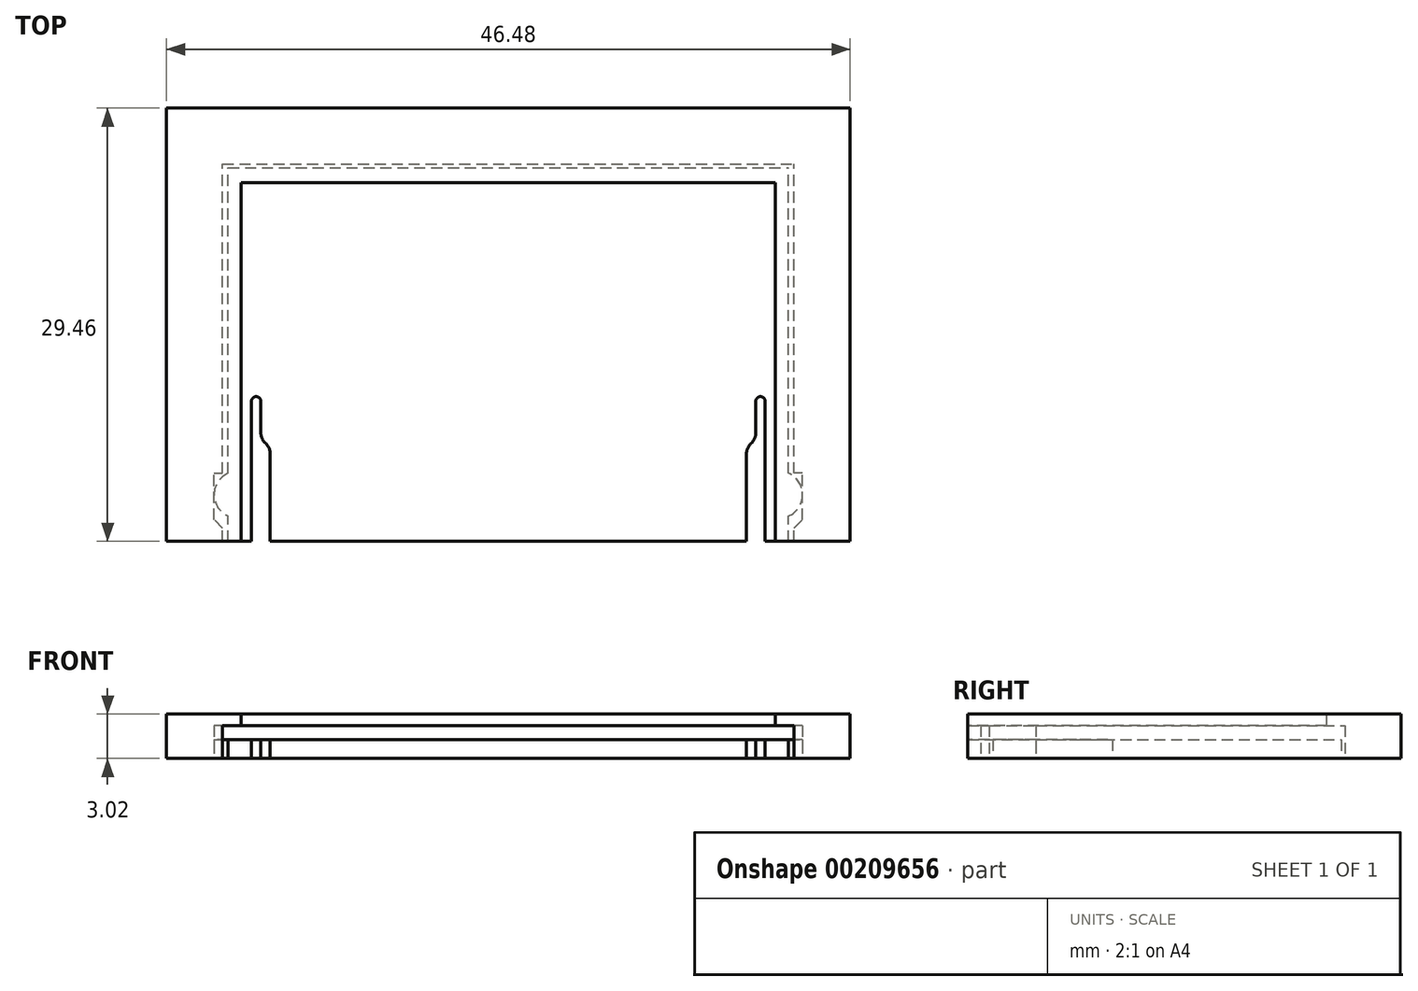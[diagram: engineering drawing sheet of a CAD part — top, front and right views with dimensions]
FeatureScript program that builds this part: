
annotation { "Feature Type Name" : "Feature", "Feature Type Description" : "" }
export const myFeature = defineFeature(function(context is Context, id is Id, definition is map)
    precondition{}
    {
        {
            var Q0;
            Q0=qCreatedBy(makeId("Top.planeOp"),FACE);
            var sketch = newSketch(context, id + "F0", { "sketchPlane" : qUnion([Q0])});
            skLineSegment(sketch, "E0", {"start": v(0, 0) * mm, "end": v(0, -25.4) * mm});
            skLineSegment(sketch, "E1", {"start": v(0, -25.4) * mm, "end": v(-16.2, -25.4) * mm});
            skLineSegment(sketch, "E2", {"start": v(-16.2, -25.4) * mm, "end": v(-16.2, -19.44) * mm});
            skLineSegment(sketch, "E3", {"start": v(-16.47, -18.77) * mm, "end": v(-16.55, -18.7) * mm});
            skLineSegment(sketch, "E4", {"start": v(-16.83, -18.02) * mm, "end": v(-16.83, -15.88) * mm});
            skLineSegment(sketch, "E5", {"start": v(-16.83, -15.88) * mm, "end": v(-17.46, -15.88) * mm, "construction": true});
            skLineSegment(sketch, "E6", {"start": v(-17.46, -15.88) * mm, "end": v(-17.46, -25.4) * mm});
            skLineSegment(sketch, "E7", {"start": v(-17.46, -25.4) * mm, "end": v(-19.05, -25.4) * mm});
            skLineSegment(sketch, "E8", {"start": v(-19.05, -25.4) * mm, "end": v(-19.05, -23.68) * mm});
            skLineSegment(sketch, "E9", {"start": v(-19.05, -20.77) * mm, "end": v(-19.05, 0) * mm});
            skLineSegment(sketch, "E10", {"start": v(-19.05, 0) * mm, "end": v(0, 0) * mm});
            skArc(sketch, "E11", {"start": v(-19.05, -20.77) * mm, "mid": v(-20, -22.23) * mm, "end": v(-19.05, -23.68) * mm});
            skArc(sketch, "E12", {"start": v(-16.83, -15.88) * mm, "mid": v(-17.14, -15.56) * mm, "end": v(-17.46, -15.88) * mm});
            skPoint(sketch, "E13.visualSharp", {"position": v(-16.83, -18.41) * mm});
            skArc(sketch, "E13.filletArc", {"start": v(-16.83, -18.02) * mm, "mid": v(-16.75, -18.38) * mm, "end": v(-16.55, -18.7) * mm});
            skPoint(sketch, "E14.visualSharp", {"position": v(-16.2, -19.05) * mm});
            skArc(sketch, "E14.filletArc", {"start": v(-16.2, -19.44) * mm, "mid": v(-16.27, -19.08) * mm, "end": v(-16.47, -18.77) * mm});
            skSolve(sketch);
        }
        {
            var Q0;
            Q0 = qSketchRegion(id + "F0", true);
            extrude(context, id + "F1", {"entities" : qUnion([Q0]), "depth" : 1.27 * mm});
        }
        {
            var Q0;
            Q0=qCreatedBy(makeId("Top.planeOp"),FACE);
            var sketch = newSketch(context, id + "F2", { "sketchPlane" : qUnion([Q0])});
            skLineSegment(sketch, "E15", {"start": v(-19.43, -25.4) * mm, "end": v(-19.43, -24.5) * mm});
            skLineSegment(sketch, "E16", {"start": v(-19.43, -24.5) * mm, "end": v(-20, -23.93) * mm});
            skLineSegment(sketch, "E17", {"start": v(-20, -23.93) * mm, "end": v(-20, -20.77) * mm});
            skLineSegment(sketch, "E18", {"start": v(-20, -20.77) * mm, "end": v(-19.43, -20.77) * mm});
            skLineSegment(sketch, "E19", {"start": v(-19.43, -20.77) * mm, "end": v(-19.43, 0.25) * mm});
            skLineSegment(sketch, "E20", {"start": v(-19.43, 0.25) * mm, "end": v(0, 0.25) * mm});
            skLineSegment(sketch, "E21", {"start": v(0, 0.25) * mm, "end": v(0, 4.06) * mm});
            skLineSegment(sketch, "E22", {"start": v(0, 4.06) * mm, "end": v(-23.24, 4.06) * mm});
            skLineSegment(sketch, "E23", {"start": v(-23.24, 4.06) * mm, "end": v(-23.24, -25.4) * mm});
            skLineSegment(sketch, "E24", {"start": v(-23.24, -25.4) * mm, "end": v(-19.43, -25.4) * mm});
            skSolve(sketch);
        }
        {
            var Q0;
            Q0 = qSketchRegion(id + "F2", true);
            extrude(context, id + "F3", {"entities" : qUnion([Q0]), "depth" : 2.22 * mm});
        }
        {
            var Q0;
            Q0=makeQuery(id+"F3.opExtrude","CAP_FACE",FACE,{"disambiguationData":[OSD([sQuery(id+"F2.wireOp",EDGE,"E15"),sQuery(id+"F2.wireOp",EDGE,"E16"),sQuery(id+"F2.wireOp",EDGE,"E17"),sQuery(id+"F2.wireOp",EDGE,"E18"),sQuery(id+"F2.wireOp",EDGE,"E19"),sQuery(id+"F2.wireOp",EDGE,"E20"),sQuery(id+"F2.wireOp",EDGE,"E21"),sQuery(id+"F2.wireOp",EDGE,"E22"),sQuery(id+"F2.wireOp",EDGE,"E23"),sQuery(id+"F2.wireOp",EDGE,"E24")])],"isStart":false});
            var sketch = newSketch(context, id + "F4", { "sketchPlane" : qUnion([Q0])});
            skLineSegment(sketch, "E25", {"start": v(0, 4.06) * mm, "end": v(0, -1.02) * mm});
            skLineSegment(sketch, "E26", {"start": v(0, -1.02) * mm, "end": v(-18.16, -1.02) * mm});
            skLineSegment(sketch, "E27", {"start": v(-18.16, -1.02) * mm, "end": v(-18.16, -25.4) * mm});
            skLineSegment(sketch, "E28", {"start": v(-18.16, -25.4) * mm, "end": v(-23.24, -25.4) * mm});
            skLineSegment(sketch, "E29", {"start": v(-23.24, -25.4) * mm, "end": v(-23.24, 4.06) * mm});
            skLineSegment(sketch, "E30", {"start": v(-23.24, 4.06) * mm, "end": v(0, 4.06) * mm});
            skSolve(sketch);
        }
        {
            var Q0;
            Q0 = qSketchRegion(id + "F4", true);
            extrude(context, id + "F5", {"entities" : qUnion([Q0]), "operationType" : NewBodyOperationType.ADD, "depth" : 0.8 * mm});
        }
        {
            var Q0;
            Q0=makeQuery(id+"F1.opExtrude","SWEPT_BODY",BODY,{"disambiguationData":[OSD([sQuery(id+"F0.wireOp",EDGE,"E0"),sQuery(id+"F0.wireOp",EDGE,"E1"),sQuery(id+"F0.wireOp",EDGE,"E2"),sQuery(id+"F0.wireOp",EDGE,"E3"),sQuery(id+"F0.wireOp",EDGE,"E4"),sQuery(id+"F0.wireOp",EDGE,"E6"),sQuery(id+"F0.wireOp",EDGE,"E7"),sQuery(id+"F0.wireOp",EDGE,"E8"),sQuery(id+"F0.wireOp",EDGE,"E9"),sQuery(id+"F0.wireOp",EDGE,"E10"),sQuery(id+"F0.wireOp",EDGE,"E11"),sQuery(id+"F0.wireOp",EDGE,"E12"),sQuery(id+"F0.wireOp",EDGE,"E13.filletArc"),sQuery(id+"F0.wireOp",EDGE,"E14.filletArc")])]});
            var Q1;
            Q1=qCreatedBy(makeId("Right.planeOp"),FACE);
            mirror(context, id + "F6", {"operationType" : NewBodyOperationType.ADD, "entities" : qUnion([Q0]), "mirrorPlane" : qUnion([Q1])});
        }
        {
            var Q0;
            Q0=makeQuery(id+"F3.opExtrude","SWEPT_BODY",BODY,{"disambiguationData":[OSD([sQuery(id+"F2.wireOp",EDGE,"E15"),sQuery(id+"F2.wireOp",EDGE,"E16"),sQuery(id+"F2.wireOp",EDGE,"E17"),sQuery(id+"F2.wireOp",EDGE,"E18"),sQuery(id+"F2.wireOp",EDGE,"E19"),sQuery(id+"F2.wireOp",EDGE,"E20"),sQuery(id+"F2.wireOp",EDGE,"E21"),sQuery(id+"F2.wireOp",EDGE,"E22"),sQuery(id+"F2.wireOp",EDGE,"E23"),sQuery(id+"F2.wireOp",EDGE,"E24")])]});
            var Q1;
            Q1=qCreatedBy(makeId("Right.planeOp"),FACE);
            mirror(context, id + "F7", {"operationType" : NewBodyOperationType.ADD, "entities" : qUnion([Q0]), "mirrorPlane" : qUnion([Q1])});
        }
    });
